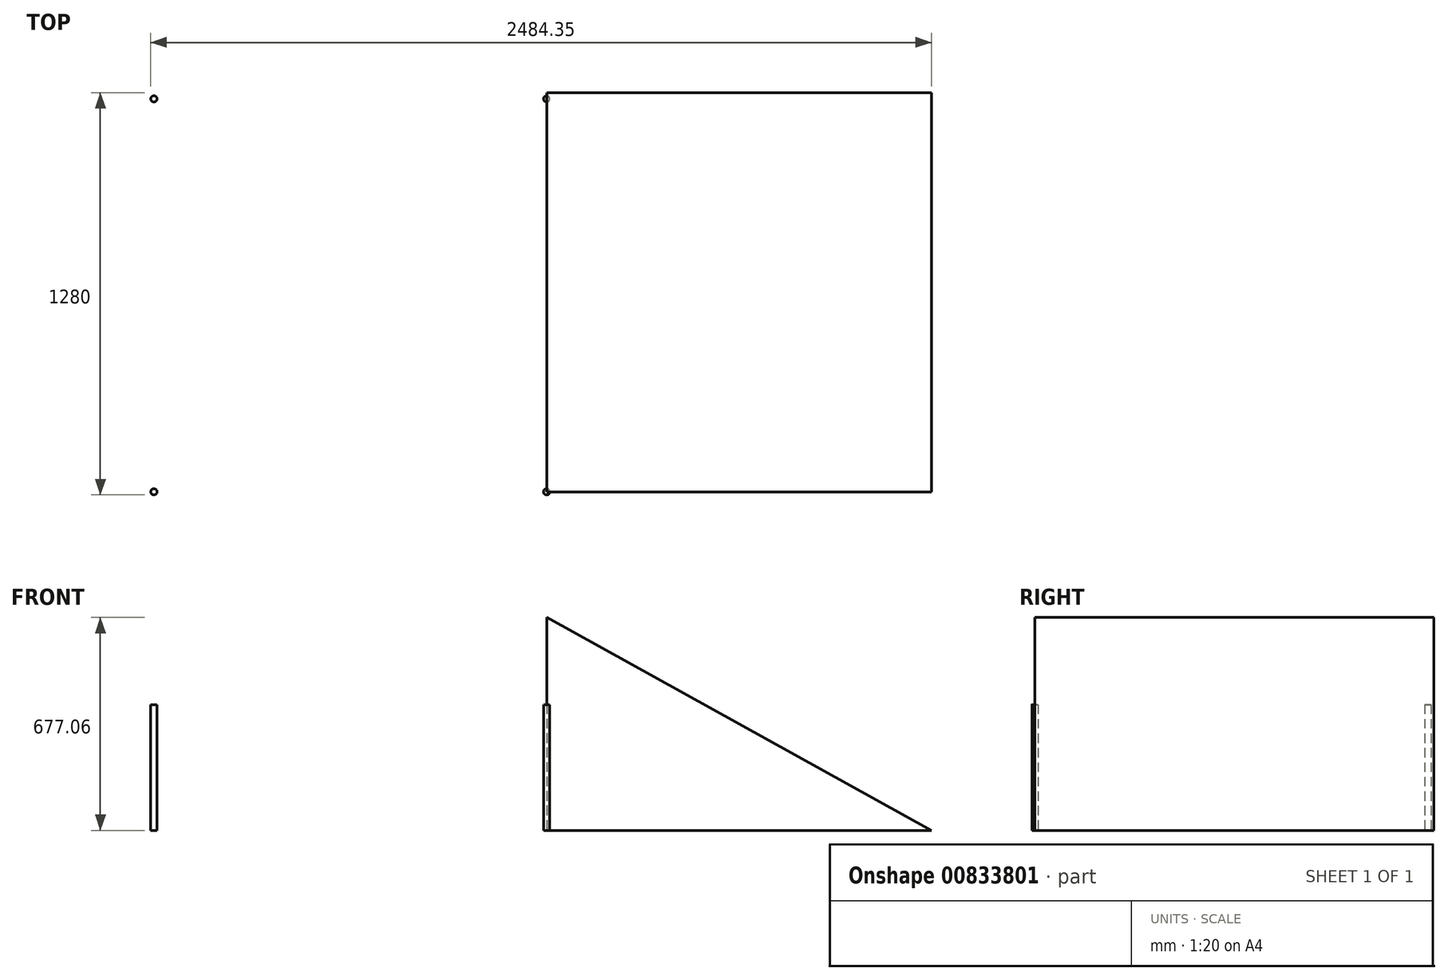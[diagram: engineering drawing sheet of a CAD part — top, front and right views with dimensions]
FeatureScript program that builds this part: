
annotation { "Feature Type Name" : "Feature", "Feature Type Description" : "" }
export const myFeature = defineFeature(function(context is Context, id is Id, definition is map)
    precondition{}
    {
        {
            var Q0;
            Q0=qCreatedBy(makeId("Top.planeOp"),FACE);
            var sketch = newSketch(context, id + "F0", { "sketchPlane" : qUnion([Q0])});
            skLineSegment(sketch, "E0", {"start": v(0, 0) * mm, "end": v(0, 1250) * mm});
            skLineSegment(sketch, "E1", {"start": v(0, 1250) * mm, "end": v(-1250, 1250) * mm});
            skLineSegment(sketch, "E2", {"start": v(-1250, 1250) * mm, "end": v(-1250, 0) * mm});
            skLineSegment(sketch, "E3", {"start": v(-1250, 0) * mm, "end": v(0, 0) * mm});
            skCircle(sketch, "E4", {"center": v(-1250, 1250) * mm, "radius": 10 * mm});
            skCircle(sketch, "E5", {"center": v(-1250, 0) * mm, "radius": 10 * mm});
            skCircle(sketch, "E6", {"center": v(0, 1250) * mm, "radius": 10 * mm});
            skCircle(sketch, "E7", {"center": v(0, 0) * mm, "radius": 10 * mm});
            skSolve(sketch);
        }
        {
            var Q0;
            {var subQ0=sQuery(id+"F0.wireOp",EDGE,"E1");var subQ1=sQuery(id+"F0.wireOp",EDGE,"E0");var subQ2=makeQuery(id+"F0.imprint","INTERSECT",VERTEX,{"derivedFrom":[subQ1,subQ0]});Q0=makeQuery(id+"F0.imprint","IMPRINT",FACE,{"disambiguationData":[TD([[makeQuery(id+"F0.imprint","IMPRINT",EDGE,{"disambiguationData":[TD([[subQ2,1.0]])],"derivedFrom":subQ1}),-1.0]])]});}
            var Q1;
            {var subQ0=sQuery(id+"F0.wireOp",EDGE,"E1");var subQ1=sQuery(id+"F0.wireOp",EDGE,"E0");var subQ2=makeQuery(id+"F0.imprint","INTERSECT",VERTEX,{"derivedFrom":[subQ1,subQ0]});Q1=makeQuery(id+"F0.imprint","IMPRINT",FACE,{"disambiguationData":[TD([[makeQuery(id+"F0.imprint","IMPRINT",EDGE,{"disambiguationData":[TD([[subQ2,1.0]])],"derivedFrom":subQ1}),1.0]])]});}
            var Q2;
            {var subQ0=sQuery(id+"F0.wireOp",EDGE,"E2");var subQ1=sQuery(id+"F0.wireOp",EDGE,"E1");var subQ2=makeQuery(id+"F0.imprint","INTERSECT",VERTEX,{"derivedFrom":[subQ1,subQ0]});Q2=makeQuery(id+"F0.imprint","IMPRINT",FACE,{"disambiguationData":[TD([[makeQuery(id+"F0.imprint","IMPRINT",EDGE,{"disambiguationData":[TD([[subQ2,1.0]])],"derivedFrom":subQ1}),-1.0]])]});}
            var Q3;
            {var subQ0=sQuery(id+"F0.wireOp",EDGE,"E2");var subQ1=sQuery(id+"F0.wireOp",EDGE,"E1");var subQ2=makeQuery(id+"F0.imprint","INTERSECT",VERTEX,{"derivedFrom":[subQ1,subQ0]});Q3=makeQuery(id+"F0.imprint","IMPRINT",FACE,{"disambiguationData":[TD([[makeQuery(id+"F0.imprint","IMPRINT",EDGE,{"disambiguationData":[TD([[subQ2,1.0]])],"derivedFrom":subQ1}),1.0]])]});}
            var Q4;
            {var subQ0=sQuery(id+"F0.wireOp",EDGE,"E3");var subQ1=sQuery(id+"F0.wireOp",EDGE,"E2");var subQ2=makeQuery(id+"F0.imprint","INTERSECT",VERTEX,{"derivedFrom":[subQ1,subQ0]});Q4=makeQuery(id+"F0.imprint","IMPRINT",FACE,{"disambiguationData":[TD([[makeQuery(id+"F0.imprint","IMPRINT",EDGE,{"disambiguationData":[TD([[subQ2,1.0]])],"derivedFrom":subQ1}),-1.0]])]});}
            var Q5;
            {var subQ0=sQuery(id+"F0.wireOp",EDGE,"E3");var subQ1=sQuery(id+"F0.wireOp",EDGE,"E2");var subQ2=makeQuery(id+"F0.imprint","INTERSECT",VERTEX,{"derivedFrom":[subQ1,subQ0]});Q5=makeQuery(id+"F0.imprint","IMPRINT",FACE,{"disambiguationData":[TD([[makeQuery(id+"F0.imprint","IMPRINT",EDGE,{"disambiguationData":[TD([[subQ2,1.0]])],"derivedFrom":subQ1}),1.0]])]});}
            var Q6;
            {var subQ0=sQuery(id+"F0.wireOp",EDGE,"E3");var subQ1=sQuery(id+"F0.wireOp",EDGE,"E0");var subQ2=makeQuery(id+"F0.imprint","INTERSECT",VERTEX,{"derivedFrom":[subQ1,subQ0]});Q6=makeQuery(id+"F0.imprint","IMPRINT",FACE,{"disambiguationData":[TD([[makeQuery(id+"F0.imprint","IMPRINT",EDGE,{"disambiguationData":[TD([[subQ2,-1.0]])],"derivedFrom":subQ1}),-1.0]])]});}
            var Q7;
            {var subQ0=sQuery(id+"F0.wireOp",EDGE,"E3");var subQ1=sQuery(id+"F0.wireOp",EDGE,"E0");var subQ2=makeQuery(id+"F0.imprint","INTERSECT",VERTEX,{"derivedFrom":[subQ1,subQ0]});Q7=makeQuery(id+"F0.imprint","IMPRINT",FACE,{"disambiguationData":[TD([[makeQuery(id+"F0.imprint","IMPRINT",EDGE,{"disambiguationData":[TD([[subQ2,-1.0]])],"derivedFrom":subQ1}),1.0]])]});}
            extrude(context, id + "F1", {"entities" : qUnion([Q0, Q1, Q2, Q3, Q4, Q5, Q6, Q7]), "depth" : 400 * mm, "offsetDistance" : 25 * mm});
        }
        {
            var Q0;
            Q0=qCreatedBy(makeId("Front.planeOp"),FACE);
            var sketch = newSketch(context, id + "F2", { "sketchPlane" : qUnion([Q0])});
            skLineSegment(sketch, "E8", {"start": v(0, 0) * mm, "end": v(1224.35, 0) * mm});
            skLineSegment(sketch, "E9", {"start": v(0, 400.34) * mm, "end": v(0, 0) * mm});
            skLineSegment(sketch, "E10", {"start": v(0, 641.1) * mm, "end": v(0, 0) * mm});
            skLineSegment(sketch, "E11", {"start": v(1224.35, 0) * mm, "end": v(0, 677.06) * mm});
            skLineSegment(sketch, "E12", {"start": v(0, 677.06) * mm, "end": v(0, 0) * mm});
            skSolve(sketch);
        }
        {
            var Q0;
            Q0=makeQuery(id+"F2.imprint","IMPRINT",FACE,{"disambiguationData":[TD([[makeQuery(id+"F2.imprint","IMPRINT",EDGE,{"derivedFrom":sQuery(id+"F2.wireOp",EDGE,"E8")}),1.0]])]});
            extrude(context, id + "F3", {"entities" : qUnion([Q0]), "oppositeDirection" : true, "depth" : 1270 * mm, "offsetDistance" : 25 * mm});
        }
    });
